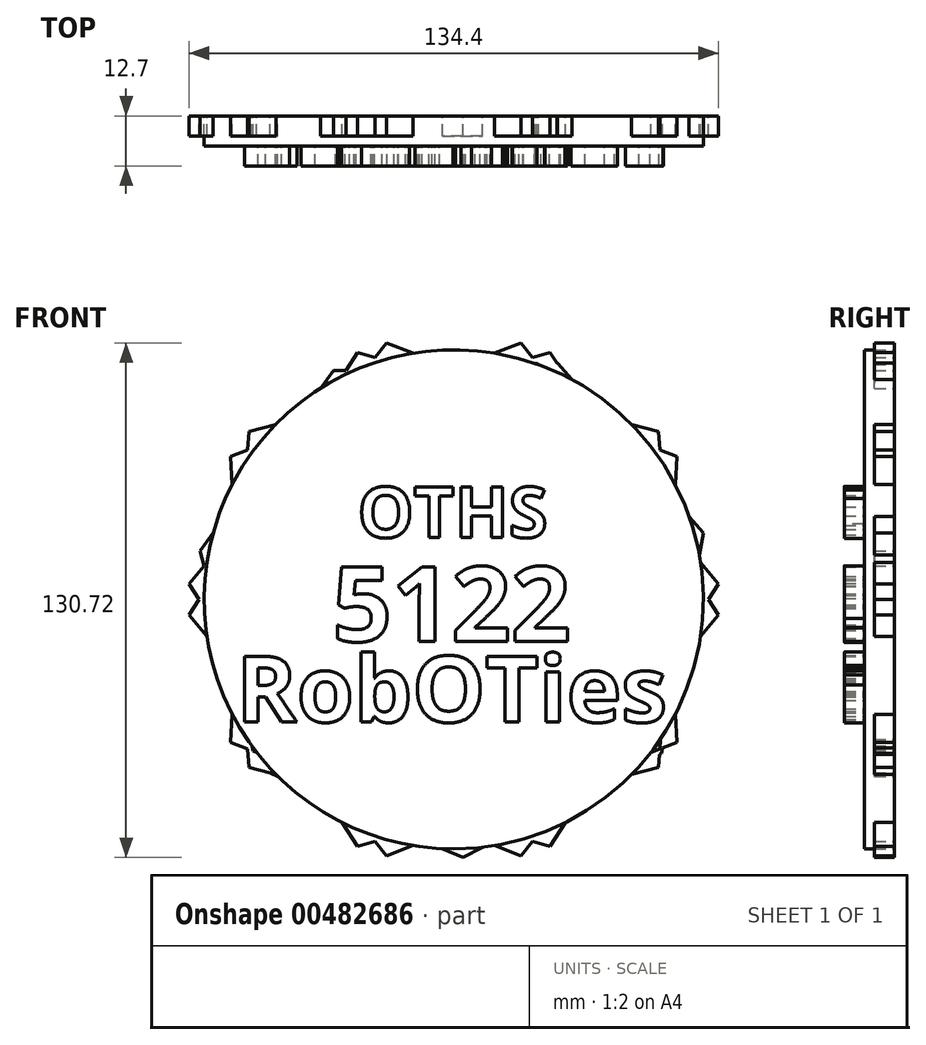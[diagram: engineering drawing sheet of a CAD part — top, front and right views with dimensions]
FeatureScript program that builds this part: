
annotation { "Feature Type Name" : "Feature", "Feature Type Description" : "" }
export const myFeature = defineFeature(function(context is Context, id is Id, definition is map)
    precondition{}
    {
        {
            var Q0;
            Q0=qCreatedBy(makeId("Front.planeOp"),FACE);
            var sketch = newSketch(context, id + "F0", { "sketchPlane" : qUnion([Q0])});
            skCircle(sketch, "E0.cCircle", {"center": v(0, 0) * mm, "radius": 63.4 * mm, "construction": true});
            skLineSegment(sketch, "E0.0", {"start": v(49.97, -39.02) * mm, "end": v(-8.8, -62.79) * mm});
            skLineSegment(sketch, "E0.1", {"start": v(-8.8, -62.79) * mm, "end": v(-58.78, -23.77) * mm});
            skLineSegment(sketch, "E0.2", {"start": v(-58.78, -23.77) * mm, "end": v(-49.97, 39.02) * mm});
            skLineSegment(sketch, "E0.3", {"start": v(-49.97, 39.02) * mm, "end": v(8.8, 62.79) * mm});
            skLineSegment(sketch, "E0.4", {"start": v(8.8, 62.79) * mm, "end": v(58.78, 23.77) * mm});
            skLineSegment(sketch, "E0.5", {"start": v(58.78, 23.77) * mm, "end": v(49.97, -39.02) * mm});
            skCircle(sketch, "E1", {"center": v(0, 0) * mm, "radius": 63.4 * mm});
            skSolve(sketch);
        }
        {
            var Q0;
            Q0 = qSketchRegion(id + "F0", true);
            extrude(context, id + "F1", {"entities" : qUnion([Q0]), "depth" : 7.62 * mm});
        }
        {
            var Q0;
            Q0=qCreatedBy(makeId("Front.planeOp"),FACE);
            var sketch = newSketch(context, id + "F2", { "sketchPlane" : qUnion([Q0])});
            skCircle(sketch, "E2.cCircle", {"center": v(0, 0) * mm, "radius": 54.46 * mm, "construction": true});
            skLineSegment(sketch, "E2.0", {"start": v(67.2, -3.94) * mm, "end": v(17.02, -65.13) * mm});
            skLineSegment(sketch, "E2.1", {"start": v(17.02, -65.13) * mm, "end": v(-56.68, -36.31) * mm});
            skLineSegment(sketch, "E2.2", {"start": v(-56.68, -36.31) * mm, "end": v(-52.05, 42.68) * mm});
            skLineSegment(sketch, "E2.3", {"start": v(-52.05, 42.68) * mm, "end": v(24.5, 62.7) * mm});
            skLineSegment(sketch, "E2.4", {"start": v(24.5, 62.7) * mm, "end": v(67.2, -3.94) * mm});
            skPoint(sketch, "E2.0.midPoint", {"position": v(42.11, -34.53) * mm});
            skLineSegment(sketch, "E3.MirrorCS", {"start": v(-52.05, -42.68) * mm, "end": v(24.5, -62.7) * mm});
            skLineSegment(sketch, "E4.MirrorCS", {"start": v(24.5, -62.7) * mm, "end": v(67.2, 3.94) * mm});
            skLineSegment(sketch, "E5.MirrorCS", {"start": v(-56.68, 36.31) * mm, "end": v(-52.05, -42.68) * mm});
            skLineSegment(sketch, "E6.MirrorCS", {"start": v(67.2, 3.94) * mm, "end": v(17.02, 65.13) * mm});
            skLineSegment(sketch, "E7.MirrorCS", {"start": v(17.02, 65.13) * mm, "end": v(-56.68, 36.31) * mm});
            skLineSegment(sketch, "E8.MirrorCS", {"start": v(-24.5, 62.7) * mm, "end": v(-67.2, -3.94) * mm});
            skLineSegment(sketch, "E9.MirrorCS", {"start": v(-67.2, 3.94) * mm, "end": v(-17.02, 65.13) * mm});
            skLineSegment(sketch, "E10.MirrorCS", {"start": v(52.05, 42.68) * mm, "end": v(-24.5, 62.7) * mm});
            skLineSegment(sketch, "E11.MirrorCS", {"start": v(-17.02, 65.13) * mm, "end": v(56.68, 36.31) * mm});
            skLineSegment(sketch, "E12.MirrorCS", {"start": v(56.68, -36.31) * mm, "end": v(52.05, 42.68) * mm});
            skLineSegment(sketch, "E13.MirrorCS", {"start": v(56.68, 36.31) * mm, "end": v(52.05, -42.68) * mm});
            skLineSegment(sketch, "E14.MirrorCS", {"start": v(-17.02, -65.13) * mm, "end": v(56.68, -36.31) * mm});
            skLineSegment(sketch, "E15.MirrorCS", {"start": v(52.05, -42.68) * mm, "end": v(-24.5, -62.7) * mm});
            skLineSegment(sketch, "E16.MirrorCS", {"start": v(-67.2, -3.94) * mm, "end": v(-17.02, -65.13) * mm});
            skLineSegment(sketch, "E17.MirrorCS", {"start": v(-24.5, -62.7) * mm, "end": v(-67.2, 3.94) * mm});
            skCircle(sketch, "E18.cCircle", {"center": v(0, 0) * mm, "radius": 59.13 * mm, "construction": true});
            skLineSegment(sketch, "E18.0", {"start": v(52.71, -39.1) * mm, "end": v(2.3, -65.59) * mm});
            skLineSegment(sketch, "E18.1", {"start": v(2.3, -65.59) * mm, "end": v(-49.84, -42.7) * mm});
            skLineSegment(sketch, "E18.2", {"start": v(-49.84, -42.7) * mm, "end": v(-64.45, 12.35) * mm});
            skLineSegment(sketch, "E18.3", {"start": v(-64.45, 12.35) * mm, "end": v(-30.53, 58.1) * mm});
            skLineSegment(sketch, "E18.4", {"start": v(-30.53, 58.1) * mm, "end": v(26.39, 60.09) * mm});
            skLineSegment(sketch, "E18.5", {"start": v(26.39, 60.09) * mm, "end": v(63.43, 16.84) * mm});
            skLineSegment(sketch, "E18.6", {"start": v(63.43, 16.84) * mm, "end": v(52.71, -39.1) * mm});
            skPoint(sketch, "E18.0.midPoint", {"position": v(27.5, -52.34) * mm});
            skSolve(sketch);
        }
        {
            var Q0;
            Q0 = qSketchRegion(id + "F2", true);
            extrude(context, id + "F3", {"entities" : qUnion([Q0]), "operationType" : NewBodyOperationType.ADD, "depth" : 5.08 * mm});
        }
        {
            var Q0;
            Q0=qCreatedBy(makeId("Front.planeOp"),FACE);
            var sketch = newSketch(context, id + "F4", { "sketchPlane" : qUnion([Q0])});
            skText(sketch, "E19", { "text": "OTHS", "fontName": "OpenSans-Bold.ttf"});
            skText(sketch, "E20", { "text": "5122", "fontName": "OpenSans-Bold.ttf"});
            skText(sketch, "E21", { "text": "RobOTies", "fontName": "OpenSans-Bold.ttf"});
            const initialGuessF4  = {"E19": [-0.02442, 0.01572, 1, 0, 0.01291], "E20": [-0.03088, -0.01067, 1, 0, 0.0191], "E21": [-0.0553, -0.03116, 1, 0, 0.01684]};
            skSetInitialGuess(sketch, initialGuessF4);
            skSolve(sketch);
        }
        {
            var Q0;
            Q0 = qSketchRegion(id + "F4", true);
            extrude(context, id + "F5", {"entities" : qUnion([Q0]), "operationType" : NewBodyOperationType.ADD, "depth" : 5.08 * mm});
        }
        {
            var Q0;
            Q0 = qSketchRegion(id + "F4", true);
            extrude(context, id + "F6", {"entities" : qUnion([Q0]), "operationType" : NewBodyOperationType.ADD, "depth" : 12.7 * mm});
        }
    });
